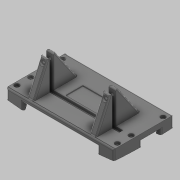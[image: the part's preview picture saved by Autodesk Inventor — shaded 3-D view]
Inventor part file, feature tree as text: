
AUTODESK INVENTOR PART (.ipt)
format: ipt  version: 2020 (Build 240168000, 168)  size: 7,906,304 bytes
history: native  units: in
note: dims shown in document units (in); Inventor stores cm internally (conversion verified against a paired STEP export)
features: sketch x16, extrude x12, plane x8, chamfer x7, other x6, fillet x4, revolve x3, split x3, hole x3, projected_geometry x2, sweep x1
ambient origin geometry x8: Origin, YZ Plane, XZ Plane, XY Plane, X Axis, Y Axis, Z Axis, Center Point
bodies: Solid7 (feature_tree), Solid8 (feature_tree), Solid10 (feature_tree)
feature tree (65):
  other  "ProfileTop"
  other  "ProfileSide"
  other  "XY_Project"
  other  "ProfileBack"
  revolve  "RevolvePlane"  [1 undecoded]
  revolve  "RevolveSketch"  [1 undecoded]
  extrude  "Extrusion5"  Depth=7.874in
  extrude  "Extrusion6"  Depth=5.4528in
  split  "Split1"
  revolve  "Revolution1"  [1 undecoded]
  chamfer  "Chamfer4"  Distance=1.8083in
  chamfer  "Chamfer5"  Distance=1.6341in
  chamfer  "Chamfer6"  Distance=0.8398in
  chamfer  "Chamfer7"  [1 undecoded]
  sweep  "Sweep1"
  chamfer  "Chamfer8"  Distance=0.1969in
  chamfer  "Chamfer9"  Distance=0.1969in
  chamfer  "Chamfer10"  Distance=29.8893in
  other  "SensorDivet"
  extrude  "Extrusion7"  Depth=0.0984in
  plane  "Work Plane6"
  plane  "Work Plane8"
  sketch  "Sketch12"  dims[d112=30.973in d142=7.874in]
  extrude  "BackSupport"  Depth=0.0984in
  extrude  "FrontSupport"  Depth=0.0984in
  plane  "Work Plane9"
  sketch  "Sketch19"  dims[d159=2.937in d160=16.7023in]
  sketch  "Sketch21"  dims[d161=16.7023in]
  extrude  "BaseVerticalExtend"  Depth=0.0984in
  plane  "Work Plane10"
  extrude  "BasePlate"  Depth=0.0984in
  extrude  "TriRib"  Depth=0.0984in
  extrude  "Slot"  Depth=0.0984in
  plane  "Work Plane11"
  extrude  "Extrusion19"  Depth=0.0984in
  extrude  "Extrusion20"  Depth=0.0984in TaperAngle=0.0deg
  hole  "Hole2"  [1 undecoded]
  fillet  "Fillet1"  [1 undecoded]
  fillet  "Fillet2"  Radius=1.4961in
  fillet  "Fillet3"  Radius=1.4961in
  plane  "Work Plane13"
  split  "Split7"
  split  "Split8"
  plane  "Work Plane15"
  hole  "Hole3"  [1 undecoded]
  plane  "Work Plane16"
  hole  "Hole4"  [1 undecoded]
  extrude  "Extrusion21"  Depth=0.0984in TaperAngle=45.0deg
  fillet  "Fillet4"  Radius=0.1969in
  other  "Image8"
  sketch  "Sketch9"  dims[d98=7.874in d109=2.278in]
  sketch  "3D Sketch1"
  sketch  "Sketch10"  dims[d110=12.4228in d111=3.715in]
  sketch  "Sketch13"  dims[d155=5.4528in d158=5.4528in]
  projected_geometry  "Projected Loop1"
  projected_geometry  "Projected Loop2"
  sketch  "Sketch22"  dims[d162=2.937in]
  sketch  "Sketch23"  dims[d170=1.8504in]
  sketch  "Sketch24"  dims[d171=7.4452in]
  sketch  "Sketch26"  dims[d172=5.4724in]
  sketch  "Sketch27"  dims[d173=0.0in]
  sketch  "Sketch29"  dims[d174=4.9332in]
  sketch  "Sketch32"  dims[d175=5.4231in]
  sketch  "Sketch33"  dims[d176=1.7487in]
  sketch  "Sketch34"  dims[d177=4.8557in d178=1.8083in d179=1.6341in d180=0.8398in d181=0.0in d187=0.5906in d188=0.1969in d189=0.1969in d272=29.8893in d278=8.1496in d279=1.2598in d280=10.9449in d281=6.8898in d282=1.2598in d283=5.4724in d284=5.4724in d285=8.1496in d288=15.748in d289=0.0in d290=15.748in d291=0.0in d346=180.0deg d347=1.4961in d348=1.4961in d349=5.4724in d350=0.1969in d351=1.4961in d352=45.0deg d353=0.1969in d354=1.4961in d355=45.0deg d356=0.1969in d357=1.4961in d358=45.0deg d359=0.1969in d360=1.4961in d361=45.0deg d362=0.0in d363=0.0in d364=0.1969in d365=1.4961in d366=45.0deg d367=0.1969in d368=1.4961in d369=45.0deg d370=0.0591in d371=1.4961in d372=45.0deg d373=-1.9685in d375=0.0in d376=0.0in d377=1.4961in d378=1.4961in d379=0.0in d380=0.6693in d381=0.6693in d382=0.6693in d383=0.6693in d384=0.6693in d385=0.6693in d386=0.5512in d387=0.9055in d388=0.0in d397=-1.9685in d424=0.3937in d425=0.0in d426=1.9685in d427=0.0in d428=12.2047in d429=3.1496in d430=6.1024in d431=0.5906in d432=12.2047in d433=6.1024in d434=1.5748in d457=0.3937in d458=0.0in d459=0.0in d460=0.5906in d461=0.0in d462=3.1496in d463=3.1496in d464=0.7874in d465=0.7874in d466=4.9213in d467=4.9213in d468=0.1969in d469=0.1969in d470=3.937in d471=0.0in d479=0.4134in d480=0.7972in d481=0.0in d482=4.2126in d483=4.2126in d484=8.6713in d485=0.0in d490=-2.3622in d491=0.7874in d492=0.7874in d493=1.1811in d494=0.0in d495=0.7874in d496=0.7874in d497=0.7874in d498=0.0in d512=0.3937in d513=0.3937in d514=0.3937in d515=0.3937in d516=0.7874in d517=0.7874in d518=0.7874in d519=0.7874in d520=0.3937in d521=0.3937in d522=0.7874in d523=0.7874in d524=0.3346in d525=0.2362in d526=0.5512in d527=0.2756in d528=90.0deg d529=2.3622in d530=0.8108in d532=0.1969in d533=0.1575in d534=0.1575in d535=1.1811in d541=1.3061in d542=3.2283in d543=3.2283in d544=0.3346in d545=0.2362in d546=0.5512in d547=0.2756in d548=90.0deg d549=2.3622in d550=0.8108in d551=0.3937in d552=0.3937in d553=0.9936in d554=3.2283in d555=3.2283in d556=0.3937in d557=0.3937in d558=0.3346in d559=0.2362in d560=0.5512in d561=0.2756in d562=90.0deg d563=2.3622in d564=0.8108in d565=1.9685in d566=0.1969in d567=1.9685in d568=3.937in d571=1.1811in d572=0.0984in d573=0.0in d574=0.0984in d163=0.0197in d164=0.0344in d165=0.0197in d166=0.0344in d440=0.0197in d441=0.0344in d442=0.0197in d443=0.0344in d449=0.0197in d450=0.0344in d451=0.0197in d452=0.0344in d540=0.0394in]
note: 8 required parameter values undecoded (feature->parameter linkage not recoverable at this tier; creation-order binding heuristic only, values carry confidence <= 0.55)